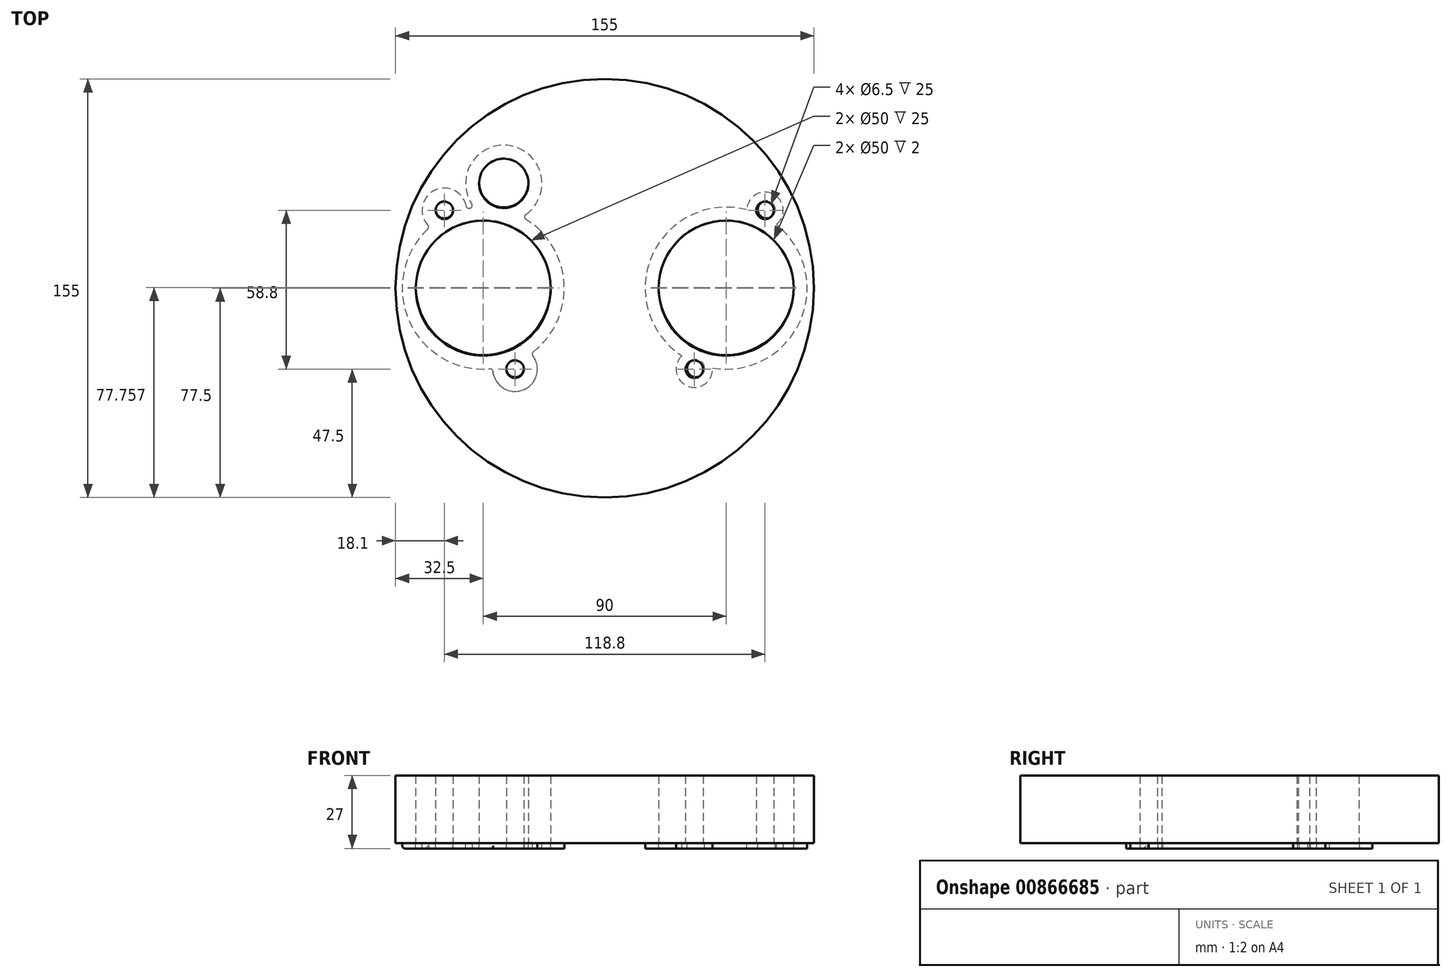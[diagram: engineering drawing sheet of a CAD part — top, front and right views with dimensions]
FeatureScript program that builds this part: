
annotation { "Feature Type Name" : "Feature", "Feature Type Description" : "" }
export const myFeature = defineFeature(function(context is Context, id is Id, definition is map)
    precondition{}
    {
        {
            var Q0;
            Q0=qCreatedBy(makeId("Top.planeOp"),FACE);
            var sketch = newSketch(context, id + "F0", { "sketchPlane" : qUnion([Q0])});
            skCircle(sketch, "E0", {"center": v(0, 0) * mm, "radius": 77.5 * mm});
            skSolve(sketch);
        }
        {
            var Q0;
            Q0=qCreatedBy(makeId("Top.planeOp"),FACE);
            var sketch = newSketch(context, id + "F1", { "sketchPlane" : qUnion([Q0])});
            skCircle(sketch, "E1", {"center": v(45, 0) * mm, "radius": 25 * mm});
            skCircle(sketch, "E2", {"center": v(-45, 0) * mm, "radius": 25 * mm});
            skCircle(sketch, "E3", {"center": v(-59.4, 28.8) * mm, "radius": 3.25 * mm});
            skCircle(sketch, "E4", {"center": v(-33.2, -30) * mm, "radius": 3.25 * mm});
            skCircle(sketch, "E5.MirrorC", {"center": v(33.2, -30) * mm, "radius": 3.25 * mm});
            skCircle(sketch, "E6.MirrorC", {"center": v(59.4, 28.8) * mm, "radius": 3.25 * mm});
            skCircle(sketch, "E7", {"center": v(-37.4, 38.8) * mm, "radius": 9.13 * mm});
            skLineSegment(sketch, "E8", {"start": v(35.65, 28.5) * mm, "end": v(35.65, 28.5) * mm});
            skSolve(sketch);
        }
        {
            var Q0;
            Q0=makeQuery(id+"F0.imprint","IMPRINT",FACE,{"disambiguationData":[TD([[makeQuery(id+"F0.imprint","IMPRINT",EDGE,{"derivedFrom":sQuery(id+"F0.wireOp",EDGE,"E0")}),1.0]])]});
            extrude(context, id + "F2", {"entities" : qUnion([Q0]), "depth" : 25 * mm, "offsetDistance" : 25 * mm});
        }
        {
            var Q0;
            Q0 = qSketchRegion(id + "F1", true);
            extrude(context, id + "F3", {"entities" : qUnion([Q0]), "operationType" : NewBodyOperationType.REMOVE, "endBound" : BoundingType.THROUGH_ALL, "depth" : 25 * mm, "offsetDistance" : 25 * mm});
        }
        {
            var Q0;
            Q0=qCreatedBy(makeId("Top.planeOp"),FACE);
            var sketch = newSketch(context, id + "F4", { "sketchPlane" : qUnion([Q0])});
            skCircle(sketch, "E9.0", {"center": v(33.2, -30) * mm, "radius": 6.75 * mm});
            skCircle(sketch, "E10.0", {"center": v(45, 0) * mm, "radius": 30 * mm});
            skCircle(sketch, "E11.0", {"center": v(59.4, 28.8) * mm, "radius": 6.75 * mm});
            skCircle(sketch, "E12.0", {"center": v(-45, 0) * mm, "radius": 30 * mm});
            skCircle(sketch, "E13.0", {"center": v(-37.4, 38.8) * mm, "radius": 14.13 * mm});
            skCircle(sketch, "E14.0", {"center": v(-59.4, 28.8) * mm, "radius": 8.25 * mm});
            skCircle(sketch, "E15.0", {"center": v(-33.2, -30) * mm, "radius": 8.25 * mm});
            skSolve(sketch);
        }
        {
            var Q0;
            Q0=qCreatedBy(makeId("Top.planeOp"),FACE);
            var sketch = newSketch(context, id + "F5", { "sketchPlane" : qUnion([Q0])});
            skCircle(sketch, "E16", {"center": v(45, 0.26) * mm, "radius": 25 * mm});
            skCircle(sketch, "E17", {"center": v(-45, 0.26) * mm, "radius": 25 * mm});
            skCircle(sketch, "E18", {"center": v(-59.4, 29.06) * mm, "radius": 3.25 * mm});
            skCircle(sketch, "E19", {"center": v(-33.2, -29.74) * mm, "radius": 3.25 * mm});
            skCircle(sketch, "E20.MirrorC", {"center": v(33.75, -29.74) * mm, "radius": 3.25 * mm});
            skCircle(sketch, "E21.MirrorC", {"center": v(59.95, 29.06) * mm, "radius": 3.25 * mm});
            skCircle(sketch, "E22", {"center": v(-37.4, 39.06) * mm, "radius": 9.13 * mm});
            skLineSegment(sketch, "E23", {"start": v(35.86, 20.4) * mm, "end": v(35.86, 20.4) * mm});
            skSolve(sketch);
        }
        {
            var Q0;
            Q0 = qSketchRegion(id + "F5", true);
            var Q1;
            Q1 = qSketchRegion(id + "F4", true);
            extrude(context, id + "F6", {"entities" : qUnion([Q0, Q1]), "operationType" : NewBodyOperationType.ADD, "oppositeDirection" : true, "depth" : 2 * mm, "offsetDistance" : 25 * mm});
        }
        {
            var Q0;
            Q0 = qSketchRegion(id + "F5", true);
            extrude(context, id + "F7", {"entities" : qUnion([Q0]), "operationType" : NewBodyOperationType.REMOVE, "endBound" : BoundingType.THROUGH_ALL, "oppositeDirection" : true, "depth" : 25 * mm, "offsetDistance" : 25 * mm});
        }
        {
            var Q0;
            {var subQ0=sQuery(id+"F4.wireOp",EDGE,"E15.0");var subQ1=sQuery(id+"F4.wireOp",EDGE,"E12.0");Q0=makeQuery(id+"F6.opExtrude","SWEPT_EDGE",EDGE,{"disambiguationData":[OSD([subQ1,subQ0]),TDD([makeQuery(id+"F4.imprint","INTERSECT",VERTEX,{"disambiguationData":[OD(1.0)],"derivedFrom":[subQ1,subQ0]})])]});}
            var Q1;
            {var subQ0=sQuery(id+"F4.wireOp",EDGE,"E15.0");var subQ1=sQuery(id+"F4.wireOp",EDGE,"E12.0");Q1=makeQuery(id+"F6.opExtrude","SWEPT_EDGE",EDGE,{"disambiguationData":[OSD([subQ1,subQ0]),TDD([makeQuery(id+"F4.imprint","INTERSECT",VERTEX,{"disambiguationData":[OD(0.0)],"derivedFrom":[subQ1,subQ0]})])]});}
            var Q2;
            {var subQ0=sQuery(id+"F4.wireOp",EDGE,"E14.0");var subQ1=sQuery(id+"F4.wireOp",EDGE,"E12.0");Q2=makeQuery(id+"F6.opExtrude","SWEPT_EDGE",EDGE,{"disambiguationData":[OSD([subQ1,subQ0]),TDD([makeQuery(id+"F4.imprint","INTERSECT",VERTEX,{"disambiguationData":[OD(1.0)],"derivedFrom":[subQ1,subQ0]})])]});}
            var Q3;
            {var subQ0=sQuery(id+"F4.wireOp",EDGE,"E14.0");var subQ1=sQuery(id+"F4.wireOp",EDGE,"E12.0");Q3=makeQuery(id+"F6.opExtrude","SWEPT_EDGE",EDGE,{"disambiguationData":[OSD([subQ1,subQ0]),TDD([makeQuery(id+"F4.imprint","INTERSECT",VERTEX,{"disambiguationData":[OD(0.0)],"derivedFrom":[subQ1,subQ0]})])]});}
            var Q4;
            {var subQ0=sQuery(id+"F4.wireOp",EDGE,"E13.0");var subQ1=sQuery(id+"F4.wireOp",EDGE,"E12.0");Q4=makeQuery(id+"F6.opExtrude","SWEPT_EDGE",EDGE,{"disambiguationData":[OSD([subQ1,subQ0]),TDD([makeQuery(id+"F4.imprint","INTERSECT",VERTEX,{"disambiguationData":[OD(0.0)],"derivedFrom":[subQ1,subQ0]})])]});}
            var Q5;
            {var subQ0=sQuery(id+"F4.wireOp",EDGE,"E13.0");var subQ1=sQuery(id+"F4.wireOp",EDGE,"E12.0");Q5=makeQuery(id+"F6.opExtrude","SWEPT_EDGE",EDGE,{"disambiguationData":[OSD([subQ1,subQ0]),TDD([makeQuery(id+"F4.imprint","INTERSECT",VERTEX,{"disambiguationData":[OD(1.0)],"derivedFrom":[subQ1,subQ0]})])]});}
            var Q6;
            {var subQ0=sQuery(id+"F4.wireOp",EDGE,"E12.0");Q6=makeQuery(id+"F6.opExtrude","CAP_EDGE",EDGE,{"disambiguationData":[OSD([subQ0]),TDD([makeQuery(id+"F4.imprint","IMPRINT",EDGE,{"disambiguationData":[TD([[makeQuery(id+"F4.imprint","INTERSECT",VERTEX,{"disambiguationData":[OD(1.0)],"derivedFrom":[subQ0,sQuery(id+"F4.wireOp",EDGE,"E14.0")]}),-1.0]])],"derivedFrom":subQ0})])],"isStart":false});}
            var Q7;
            {var subQ0=sQuery(id+"F4.wireOp",EDGE,"E12.0");Q7=makeQuery(id+"F6.opExtrude","CAP_EDGE",EDGE,{"disambiguationData":[OSD([subQ0]),TDD([makeQuery(id+"F4.imprint","IMPRINT",EDGE,{"disambiguationData":[TD([[makeQuery(id+"F4.imprint","INTERSECT",VERTEX,{"disambiguationData":[OD(1.0)],"derivedFrom":[subQ0,sQuery(id+"F4.wireOp",EDGE,"E14.0")]}),-1.0]])],"derivedFrom":subQ0})])],"isStart":true});}
            var Q8;
            {var subQ0=sQuery(id+"F4.wireOp",EDGE,"E12.0");Q8=makeQuery(id+"F6.opExtrude","CAP_EDGE",EDGE,{"disambiguationData":[OSD([subQ0]),TDD([makeQuery(id+"F4.imprint","IMPRINT",EDGE,{"disambiguationData":[TD([[makeQuery(id+"F4.imprint","INTERSECT",VERTEX,{"disambiguationData":[OD(1.0)],"derivedFrom":[subQ0,sQuery(id+"F4.wireOp",EDGE,"E13.0")]}),1.0]])],"derivedFrom":subQ0})])],"isStart":true});}
            var Q9;
            Q9=makeQuery(id+"F6.opExtrude","CAP_EDGE",EDGE,{"disambiguationData":[OSD([sQuery(id+"F4.wireOp",EDGE,"E15.0")])],"isStart":true});
            var Q10;
            Q10=makeQuery(id+"F6.opExtrude","CAP_EDGE",EDGE,{"disambiguationData":[OSD([sQuery(id+"F4.wireOp",EDGE,"E13.0")])],"isStart":true});
            var Q11;
            Q11=makeQuery(id+"F6.opExtrude","CAP_EDGE",EDGE,{"disambiguationData":[OSD([sQuery(id+"F4.wireOp",EDGE,"E14.0")])],"isStart":true});
            fillet(context, id + "F8", {"entities" : qUnion([Q0, Q1, Q2, Q3, Q4, Q5, Q6, Q7, Q8, Q9, Q10, Q11]), "radius" : 1 * mm, "tangentPropagation" : true, "allowEdgeOverflow" : false});
        }
    });
